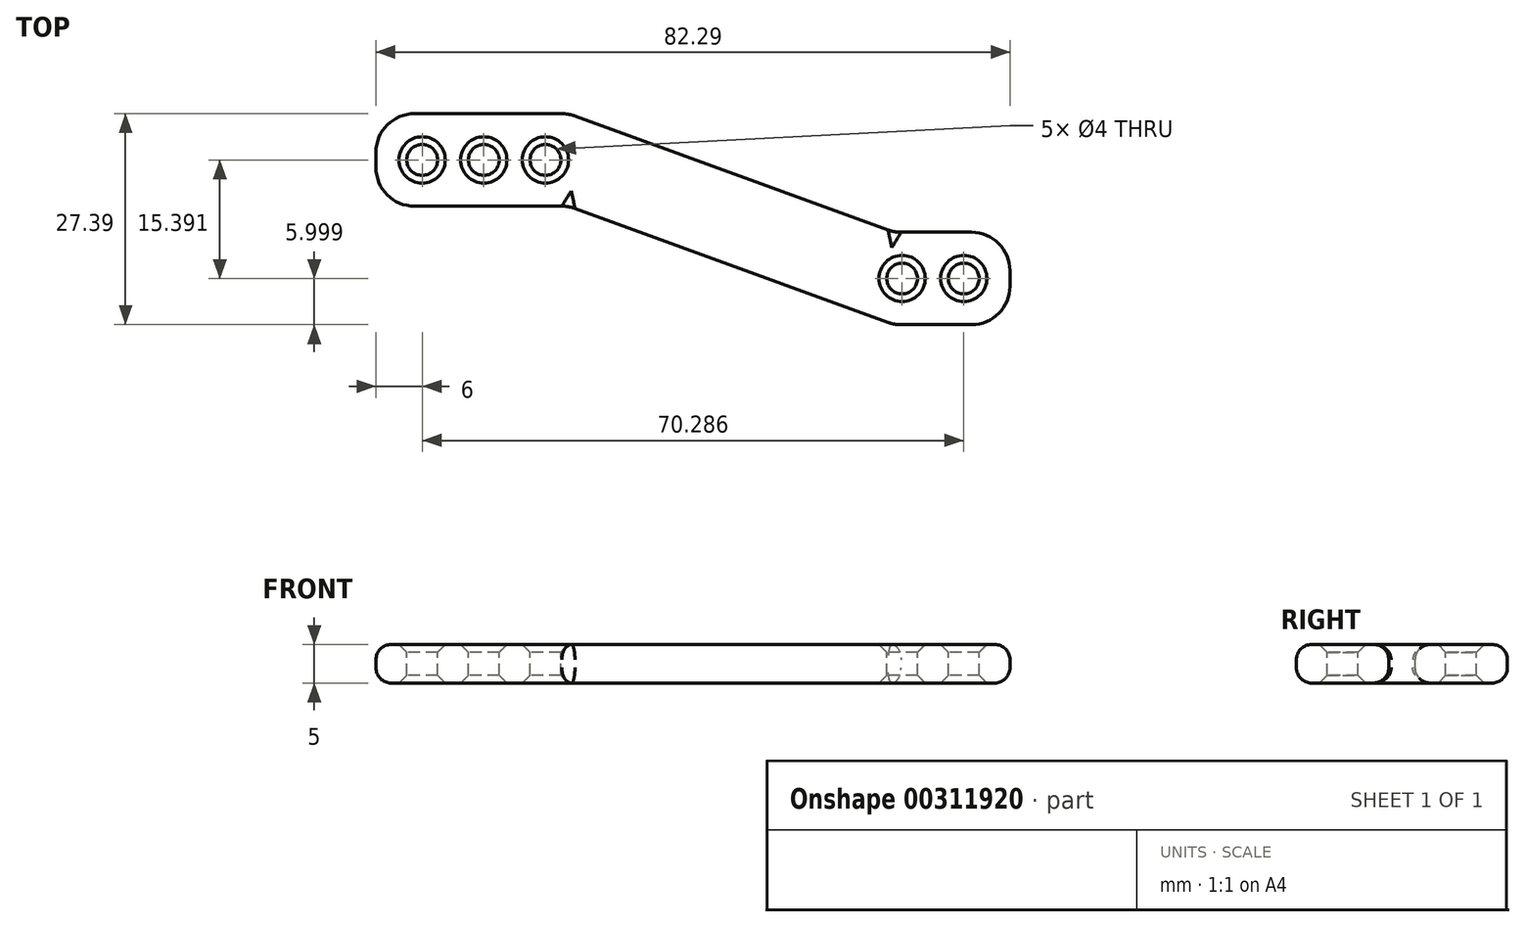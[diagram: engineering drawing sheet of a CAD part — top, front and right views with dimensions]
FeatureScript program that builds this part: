
annotation { "Feature Type Name" : "Feature", "Feature Type Description" : "" }
export const myFeature = defineFeature(function(context is Context, id is Id, definition is map)
    precondition{}
    {
        {
            var Q0;
            Q0=qCreatedBy(makeId("Top.planeOp"),FACE);
            var sketch = newSketch(context, id + "F0", { "sketchPlane" : qUnion([Q0])});
            skLineSegment(sketch, "E0.bottom", {"start": v(0, 12) * mm, "end": v(25, 12) * mm});
            skLineSegment(sketch, "E0.top", {"start": v(0, 0) * mm, "end": v(25, 0) * mm});
            skLineSegment(sketch, "E0.left", {"start": v(0, 12) * mm, "end": v(0, 0) * mm});
            skLineSegment(sketch, "E0.right", {"start": v(25, 12) * mm, "end": v(25, 0) * mm});
            skLineSegment(sketch, "E1.bottom", {"start": v(67.29, -3.4) * mm, "end": v(82.29, -3.4) * mm});
            skLineSegment(sketch, "E1.top", {"start": v(67.29, -15.4) * mm, "end": v(82.29, -15.4) * mm});
            skLineSegment(sketch, "E1.left", {"start": v(67.29, -3.4) * mm, "end": v(67.29, -15.4) * mm});
            skLineSegment(sketch, "E1.right", {"start": v(82.29, -3.4) * mm, "end": v(82.29, -15.4) * mm});
            skLineSegment(sketch, "E2", {"start": v(25, 12) * mm, "end": v(67.29, -3.4) * mm});
            skLineSegment(sketch, "E3", {"start": v(25, 0) * mm, "end": v(67.29, -15.4) * mm});
            skSolve(sketch);
        }
        {
            var Q0;
            Q0=makeQuery(id+"F0.imprint","IMPRINT",FACE,{"disambiguationData":[TD([[makeQuery(id+"F0.imprint","IMPRINT",EDGE,{"derivedFrom":sQuery(id+"F0.wireOp",EDGE,"E0.right")}),1.0]])]});
            var Q1;
            Q1=makeQuery(id+"F0.imprint","IMPRINT",FACE,{"disambiguationData":[TD([[makeQuery(id+"F0.imprint","IMPRINT",EDGE,{"derivedFrom":sQuery(id+"F0.wireOp",EDGE,"E0.bottom")}),-1.0]])]});
            var Q2;
            Q2=makeQuery(id+"F0.imprint","IMPRINT",FACE,{"disambiguationData":[TD([[makeQuery(id+"F0.imprint","IMPRINT",EDGE,{"derivedFrom":sQuery(id+"F0.wireOp",EDGE,"E1.bottom")}),-1.0]])]});
            extrude(context, id + "F1", {"entities" : qUnion([Q0, Q1, Q2]), "depth" : 5 * mm});
        }
        {
            var Q0;
            Q0=makeQuery(id+"F1.opExtrude","CAP_FACE",FACE,{"disambiguationData":[OSD([sQuery(id+"F0.wireOp",EDGE,"E0.bottom"),sQuery(id+"F0.wireOp",EDGE,"E0.top"),sQuery(id+"F0.wireOp",EDGE,"E0.left"),sQuery(id+"F0.wireOp",EDGE,"E1.bottom"),sQuery(id+"F0.wireOp",EDGE,"E1.top"),sQuery(id+"F0.wireOp",EDGE,"E1.right"),sQuery(id+"F0.wireOp",EDGE,"E2"),sQuery(id+"F0.wireOp",EDGE,"E3")])],"isStart":false});
            var sketch = newSketch(context, id + "F2", { "sketchPlane" : qUnion([Q0])});
            skCircle(sketch, "E4", {"center": v(6, 6) * mm, "radius": 2 * mm});
            skCircle(sketch, "E5", {"center": v(76.29, -9.4) * mm, "radius": 2 * mm});
            skCircle(sketch, "E6.1.0.0", {"center": v(14, 6) * mm, "radius": 2 * mm});
            skCircle(sketch, "E6.2.0.0", {"center": v(22, 6) * mm, "radius": 2 * mm});
            skLineSegment(sketch, "E6.direction1", {"start": v(6, 6) * mm, "end": v(14, 6) * mm, "construction": true});
            skCircle(sketch, "E7.1.0.0", {"center": v(68.29, -9.4) * mm, "radius": 2 * mm});
            skLineSegment(sketch, "E7.direction1", {"start": v(68.29, -9.4) * mm, "end": v(76.29, -9.4) * mm, "construction": true});
            skSolve(sketch);
        }
        {
            var Q0;
            Q0=makeQuery(id+"F2.imprint","IMPRINT",FACE,{"disambiguationData":[TD([[makeQuery(id+"F2.imprint","IMPRINT",EDGE,{"derivedFrom":sQuery(id+"F2.wireOp",EDGE,"E4")}),1.0]])]});
            var Q1;
            Q1=makeQuery(id+"F2.imprint","IMPRINT",FACE,{"disambiguationData":[TD([[makeQuery(id+"F2.imprint","IMPRINT",EDGE,{"derivedFrom":sQuery(id+"F2.wireOp",EDGE,"E6.1.0.0")}),1.0]])]});
            var Q2;
            Q2=makeQuery(id+"F2.imprint","IMPRINT",FACE,{"disambiguationData":[TD([[makeQuery(id+"F2.imprint","IMPRINT",EDGE,{"derivedFrom":sQuery(id+"F2.wireOp",EDGE,"E6.2.0.0")}),1.0]])]});
            var Q3;
            Q3=makeQuery(id+"F2.imprint","IMPRINT",FACE,{"disambiguationData":[TD([[makeQuery(id+"F2.imprint","IMPRINT",EDGE,{"derivedFrom":sQuery(id+"F2.wireOp",EDGE,"E7.1.0.0")}),1.0]])]});
            var Q4;
            Q4=makeQuery(id+"F2.imprint","IMPRINT",FACE,{"disambiguationData":[TD([[makeQuery(id+"F2.imprint","IMPRINT",EDGE,{"derivedFrom":sQuery(id+"F2.wireOp",EDGE,"E5")}),1.0]])]});
            extrude(context, id + "F3", {"entities" : qUnion([Q0, Q1, Q2, Q3, Q4]), "operationType" : NewBodyOperationType.REMOVE, "oppositeDirection" : true, "depth" : 25 * mm});
        }
        {
            var Q0;
            Q0=makeQuery(id+"F1.opExtrude","CAP_EDGE",EDGE,{"disambiguationData":[OSD([sQuery(id+"F0.wireOp",EDGE,"E0.bottom")])],"isStart":false});
            var Q1;
            Q1=makeQuery(id+"F1.opExtrude","CAP_EDGE",EDGE,{"disambiguationData":[OSD([sQuery(id+"F0.wireOp",EDGE,"E2")])],"isStart":false});
            var Q2;
            Q2=makeQuery(id+"F1.opExtrude","CAP_EDGE",EDGE,{"disambiguationData":[OSD([sQuery(id+"F0.wireOp",EDGE,"E3")])],"isStart":false});
            var Q3;
            Q3=makeQuery(id+"F1.opExtrude","CAP_EDGE",EDGE,{"disambiguationData":[OSD([sQuery(id+"F0.wireOp",EDGE,"E0.top")])],"isStart":false});
            var Q4;
            Q4=makeQuery(id+"F1.opExtrude","CAP_EDGE",EDGE,{"disambiguationData":[OSD([sQuery(id+"F0.wireOp",EDGE,"E1.right")])],"isStart":false});
            var Q5;
            Q5=makeQuery(id+"F1.opExtrude","CAP_EDGE",EDGE,{"disambiguationData":[OSD([sQuery(id+"F0.wireOp",EDGE,"E1.bottom")])],"isStart":false});
            var Q6;
            Q6=makeQuery(id+"F1.opExtrude","CAP_EDGE",EDGE,{"disambiguationData":[OSD([sQuery(id+"F0.wireOp",EDGE,"E1.top")])],"isStart":false});
            var Q7;
            Q7=makeQuery(id+"F1.opExtrude","CAP_EDGE",EDGE,{"disambiguationData":[OSD([sQuery(id+"F0.wireOp",EDGE,"E0.left")])],"isStart":false});
            fillet(context, id + "F4", {"entities" : qUnion([Q0, Q1, Q2, Q3, Q4, Q5, Q6, Q7]), "radius" : 2 * mm, "tangentPropagation" : true, "allowEdgeOverflow" : false});
        }
        {
            var Q0;
            Q0=makeQuery(id+"F1.opExtrude","CAP_EDGE",EDGE,{"disambiguationData":[OSD([sQuery(id+"F0.wireOp",EDGE,"E0.top")])],"isStart":true});
            var Q1;
            Q1=makeQuery(id+"F1.opExtrude","CAP_EDGE",EDGE,{"disambiguationData":[OSD([sQuery(id+"F0.wireOp",EDGE,"E0.left")])],"isStart":true});
            var Q2;
            Q2=makeQuery(id+"F1.opExtrude","CAP_EDGE",EDGE,{"disambiguationData":[OSD([sQuery(id+"F0.wireOp",EDGE,"E0.bottom")])],"isStart":true});
            var Q3;
            Q3=makeQuery(id+"F1.opExtrude","CAP_EDGE",EDGE,{"disambiguationData":[OSD([sQuery(id+"F0.wireOp",EDGE,"E2")])],"isStart":true});
            var Q4;
            Q4=makeQuery(id+"F1.opExtrude","CAP_EDGE",EDGE,{"disambiguationData":[OSD([sQuery(id+"F0.wireOp",EDGE,"E3")])],"isStart":true});
            var Q5;
            Q5=makeQuery(id+"F1.opExtrude","CAP_EDGE",EDGE,{"disambiguationData":[OSD([sQuery(id+"F0.wireOp",EDGE,"E1.top")])],"isStart":true});
            var Q6;
            Q6=makeQuery(id+"F1.opExtrude","CAP_EDGE",EDGE,{"disambiguationData":[OSD([sQuery(id+"F0.wireOp",EDGE,"E1.bottom")])],"isStart":true});
            var Q7;
            Q7=makeQuery(id+"F1.opExtrude","CAP_EDGE",EDGE,{"disambiguationData":[OSD([sQuery(id+"F0.wireOp",EDGE,"E1.right")])],"isStart":true});
            fillet(context, id + "F5", {"entities" : qUnion([Q0, Q1, Q2, Q3, Q4, Q5, Q6, Q7]), "radius" : 2 * mm, "tangentPropagation" : true, "allowEdgeOverflow" : false});
        }
        {
            var Q0;
            Q0=makeQuery(id+"F4.opFillet","BLEND_EDGE",EDGE,{"blendedFrom":[makeQuery(id+"F1.opExtrude","CAP_EDGE",EDGE,{"disambiguationData":[OSD([sQuery(id+"F0.wireOp",EDGE,"E0.top")])],"isStart":false}),makeQuery(id+"F1.opExtrude","CAP_EDGE",EDGE,{"disambiguationData":[OSD([sQuery(id+"F0.wireOp",EDGE,"E3")])],"isStart":false})],"blendedInto":[]});
            var Q1;
            Q1=makeQuery(id+"F1.opExtrude","SWEPT_EDGE",EDGE,{"disambiguationData":[OSD([sQuery(id+"F0.wireOp",EDGE,"E1.top"),sQuery(id+"F0.wireOp",EDGE,"E1.right")])]});
            fillet(context, id + "F6", {"entities" : qUnion([Q0, Q1]), "radius" : 5 * mm, "tangentPropagation" : true, "allowEdgeOverflow" : false});
        }
        {
            var Q0;
            Q0=makeQuery(id+"F1.opExtrude","SWEPT_EDGE",EDGE,{"disambiguationData":[OSD([sQuery(id+"F0.wireOp",EDGE,"E1.bottom"),sQuery(id+"F0.wireOp",EDGE,"E1.right")])]});
            var Q1;
            Q1=makeQuery(id+"F1.opExtrude","SWEPT_EDGE",EDGE,{"disambiguationData":[OSD([sQuery(id+"F0.wireOp",EDGE,"E0.bottom"),sQuery(id+"F0.wireOp",EDGE,"E0.left")])]});
            var Q2;
            Q2=makeQuery(id+"F1.opExtrude","SWEPT_EDGE",EDGE,{"disambiguationData":[OSD([sQuery(id+"F0.wireOp",EDGE,"E0.top"),sQuery(id+"F0.wireOp",EDGE,"E0.left")])]});
            fillet(context, id + "F7", {"entities" : qUnion([Q0, Q1, Q2]), "radius" : 5 * mm, "tangentPropagation" : true, "allowEdgeOverflow" : false});
        }
        {
            var Q0;
            Q0=makeQuery(id+"F1.opExtrude","SWEPT_EDGE",EDGE,{"disambiguationData":[OSD([sQuery(id+"F0.wireOp",EDGE,"E1.top"),sQuery(id+"F0.wireOp",EDGE,"E1.left"),sQuery(id+"F0.wireOp",EDGE,"E3")])]});
            var Q1;
            Q1=makeQuery(id+"F1.opExtrude","SWEPT_EDGE",EDGE,{"disambiguationData":[OSD([sQuery(id+"F0.wireOp",EDGE,"E1.bottom"),sQuery(id+"F0.wireOp",EDGE,"E1.left"),sQuery(id+"F0.wireOp",EDGE,"E2")])]});
            var Q2;
            {var subQ0=sQuery(id+"F0.wireOp",EDGE,"E1.bottom");Q2=makeQuery(id+"F7.opFillet","BLEND_EDGE",EDGE,{"blendedFrom":[makeQuery(id+"F1.opExtrude","SWEPT_EDGE",EDGE,{"disambiguationData":[OSD([subQ0,sQuery(id+"F0.wireOp",EDGE,"E1.right")])]}),makeQuery(id+"F1.opExtrude","SWEPT_FACE",FACE,{"disambiguationData":[OSD([subQ0])]})],"blendedInto":[makeQuery(id+"F1.opExtrude","SWEPT_FACE",FACE,{"disambiguationData":[OSD([subQ0])]})]});}
            var Q3;
            {var subQ0=sQuery(id+"F0.wireOp",EDGE,"E0.bottom");Q3=makeQuery(id+"F7.opFillet","BLEND_EDGE",EDGE,{"blendedFrom":[makeQuery(id+"F1.opExtrude","SWEPT_EDGE",EDGE,{"disambiguationData":[OSD([subQ0,sQuery(id+"F0.wireOp",EDGE,"E0.left")])]}),makeQuery(id+"F1.opExtrude","SWEPT_FACE",FACE,{"disambiguationData":[OSD([subQ0])]})],"blendedInto":[makeQuery(id+"F1.opExtrude","SWEPT_FACE",FACE,{"disambiguationData":[OSD([subQ0])]})]});}
            var Q4;
            {var subQ0=sQuery(id+"F0.wireOp",EDGE,"E0.top");Q4=makeQuery(id+"F7.opFillet","BLEND_EDGE",EDGE,{"blendedFrom":[makeQuery(id+"F1.opExtrude","SWEPT_EDGE",EDGE,{"disambiguationData":[OSD([subQ0,sQuery(id+"F0.wireOp",EDGE,"E0.left")])]}),makeQuery(id+"F1.opExtrude","SWEPT_FACE",FACE,{"disambiguationData":[OSD([subQ0])]})],"blendedInto":[makeQuery(id+"F1.opExtrude","SWEPT_FACE",FACE,{"disambiguationData":[OSD([subQ0])]})]});}
            var Q5;
            {var subQ0=sQuery(id+"F0.wireOp",EDGE,"E0.top");Q5=makeQuery(id+"F6.opFillet","BLEND_EDGE",EDGE,{"blendedFrom":[makeQuery(id+"F1.opExtrude","SWEPT_EDGE",EDGE,{"disambiguationData":[OSD([subQ0,sQuery(id+"F0.wireOp",EDGE,"E0.right"),sQuery(id+"F0.wireOp",EDGE,"E3")])]}),makeQuery(id+"F1.opExtrude","SWEPT_FACE",FACE,{"disambiguationData":[OSD([subQ0])]})],"blendedInto":[makeQuery(id+"F1.opExtrude","SWEPT_FACE",FACE,{"disambiguationData":[OSD([subQ0])]})]});}
            var Q6;
            {var subQ0=sQuery(id+"F0.wireOp",EDGE,"E3");Q6=makeQuery(id+"F6.opFillet","BLEND_EDGE",EDGE,{"blendedFrom":[makeQuery(id+"F1.opExtrude","SWEPT_EDGE",EDGE,{"disambiguationData":[OSD([sQuery(id+"F0.wireOp",EDGE,"E0.top"),sQuery(id+"F0.wireOp",EDGE,"E0.right"),subQ0])]}),makeQuery(id+"F1.opExtrude","SWEPT_FACE",FACE,{"disambiguationData":[OSD([subQ0])]})],"blendedInto":[makeQuery(id+"F1.opExtrude","SWEPT_FACE",FACE,{"disambiguationData":[OSD([subQ0])]})]});}
            fillet(context, id + "F8", {"entities" : qUnion([Q0, Q1, Q2, Q3, Q4, Q5, Q6]), "radius" : 5 * mm, "tangentPropagation" : true, "allowEdgeOverflow" : false});
        }
        {
            var Q0;
            Q0=makeQuery(id+"F1.opExtrude","SWEPT_EDGE",EDGE,{"disambiguationData":[OSD([sQuery(id+"F0.wireOp",EDGE,"E0.bottom"),sQuery(id+"F0.wireOp",EDGE,"E0.right"),sQuery(id+"F0.wireOp",EDGE,"E2")])]});
            fillet(context, id + "F9", {"entities" : qUnion([Q0]), "radius" : 5 * mm, "tangentPropagation" : true, "allowEdgeOverflow" : false});
        }
        {
            var Q0;
            Q0=makeQuery(id+"F3.boolean.opBoolean","COPY",FACE,{"derivedFrom":makeQuery(id+"F3.opExtrude","SWEPT_FACE",FACE,{"disambiguationData":[OSD([sQuery(id+"F2.wireOp",EDGE,"E4")])]})});
            var Q1;
            Q1=makeQuery(id+"F3.boolean.opBoolean","COPY",FACE,{"derivedFrom":makeQuery(id+"F3.opExtrude","SWEPT_FACE",FACE,{"disambiguationData":[OSD([sQuery(id+"F2.wireOp",EDGE,"E6.1.0.0")])]})});
            var Q2;
            Q2=makeQuery(id+"F3.boolean.opBoolean","COPY",EDGE,{"derivedFrom":makeQuery(id+"F3.opExtrude","CAP_EDGE",EDGE,{"disambiguationData":[OSD([sQuery(id+"F2.wireOp",EDGE,"E6.2.0.0")])],"isStart":true})});
            var Q3;
            Q3=makeQuery(id+"F3.boolean.opBoolean","COPY",EDGE,{"derivedFrom":makeQuery(id+"F3.opExtrude","CAP_EDGE",EDGE,{"disambiguationData":[OSD([sQuery(id+"F2.wireOp",EDGE,"E7.1.0.0")])],"isStart":true})});
            var Q4;
            Q4=makeQuery(id+"F3.boolean.opBoolean","COPY",FACE,{"derivedFrom":makeQuery(id+"F3.opExtrude","SWEPT_FACE",FACE,{"disambiguationData":[OSD([sQuery(id+"F2.wireOp",EDGE,"E7.1.0.0")])]})});
            var Q5;
            Q5=makeQuery(id+"F3.boolean.opBoolean","COPY",FACE,{"derivedFrom":makeQuery(id+"F3.opExtrude","SWEPT_FACE",FACE,{"disambiguationData":[OSD([sQuery(id+"F2.wireOp",EDGE,"E6.2.0.0")])]})});
            var Q6;
            Q6=makeQuery(id+"F3.boolean.opBoolean","COPY",FACE,{"derivedFrom":makeQuery(id+"F3.opExtrude","SWEPT_FACE",FACE,{"disambiguationData":[OSD([sQuery(id+"F2.wireOp",EDGE,"E5")])]})});
            chamfer(context, id + "F10", {"entities" : qUnion([Q0, Q1, Q2, Q3, Q4, Q5, Q6]), "width" : 1 * mm, "tangentPropagation" : true});
        }
    });
